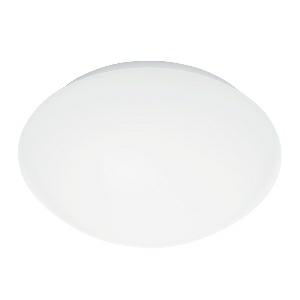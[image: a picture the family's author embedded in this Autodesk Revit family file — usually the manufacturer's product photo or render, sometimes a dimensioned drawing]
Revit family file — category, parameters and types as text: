
# Revit family: rs_pro_led_p2_sl_056087
name_source: partatom
category: Leuchten
revit_build: Autodesk Revit 2016 (Build: 20190508_0715(x64)
units: mm (PartAtom-declared; Revit-internal decimal feet)

## family parameters
Basisbauteil = Fläche
Beim Laden mit Abzugskörper schneiden = Nein
Bemaßung runder Anschluss = Durchmesser verwenden
Gemeinsam genutzt = Nein
Lichtquelle = Nein
Raumberechnungspunkt = Nein
Teiletyp = Normal

## types (1)
- RS PRO LED P2 SL (1 x , 1810 lm, 4000 K)
    Beschreibung = Dimensions (Ø x H): 320 x 110 mm; Mains power supply: 220 – 240 V / 50 – 60 Hz; Output: 15,5 W; Luminous flux: 1810 lm; Colour temperature: 4000 K; Colour variation LED: SDCM3; Colour Rendering Index CRI: 80-89; With lamp: Yes, STEINEL LED system; Lamp: LED cannot be replaced; LED life expectancy (max. °C): 50000 h; Drop in luminous flux in accordance with LM80: L80B10; Base: without; LED cooling system: Passive Thermo Control; With motion detector: No; Photo-cell controller: No; Basic light level function: No; Soft light start: Yes; Impact resistance: IK03; IP-rating: IP54; Protection class: II; Ambient temperature: 10 – 40 °C; Housing material: Plastic; Cover material: Plastic, opal; Manufacturer's Warranty: 5 years; With remote control: No; Version: Neutral white; PU1, EAN: 4007841056087
    CIE Flux Codes = 39 68 87 86 100
    Color Rendering = 80-89
    Color Temperature = 4000 K
    Frequency = 60 Hz, 50 Hz
    Height = 0 mm  [stored 0 ft]
    Hersteller = Steinel
    Lamp Light Flux = 1810 lm
    Lamp count = 1
    Lampe = 1 x
    Length = 320 mm
    Luminous efficacy = 121 lm/W
    ModVariant = Nein
    Modell = 056087
    Mounting Type = Surface mounted
    Number of Poles = 1
    OnlyDefault = Ja
    Power Factor = 1
    Product Name = RS PRO LED P2 SL
    Product group = Sensor-switched indoor light
    ProductGroupID = 30
    Protection Class = Protection class II
    Protection Degree = IP 54
    RlxData = <blob elided: 35893 chars, md5=7115d0d5>
    Scheinlast = 15 VA
    Socket = socket
    Standby Power = 0 W
    System Light Flux = 1810 lm
    System Power = 15 W
    Typenbild = produkt1_056087.jpg
    Typenkommentare = Product without accessories
    URL = http://relux.com
    VarID = ---
    Voltage = 0 V
    Vorgabe-Ansicht = 1800 mm
    Weight = 0.00 kg
    Width = 0 mm  [stored 0 ft]

note: [stored X ft] marks values corroborated as IEEE doubles in the binary element streams (Revit-internal decimal feet)

## geometry (parser evidence)
native form markers: Sweep x14
no freeform markers — native parametric forms only
